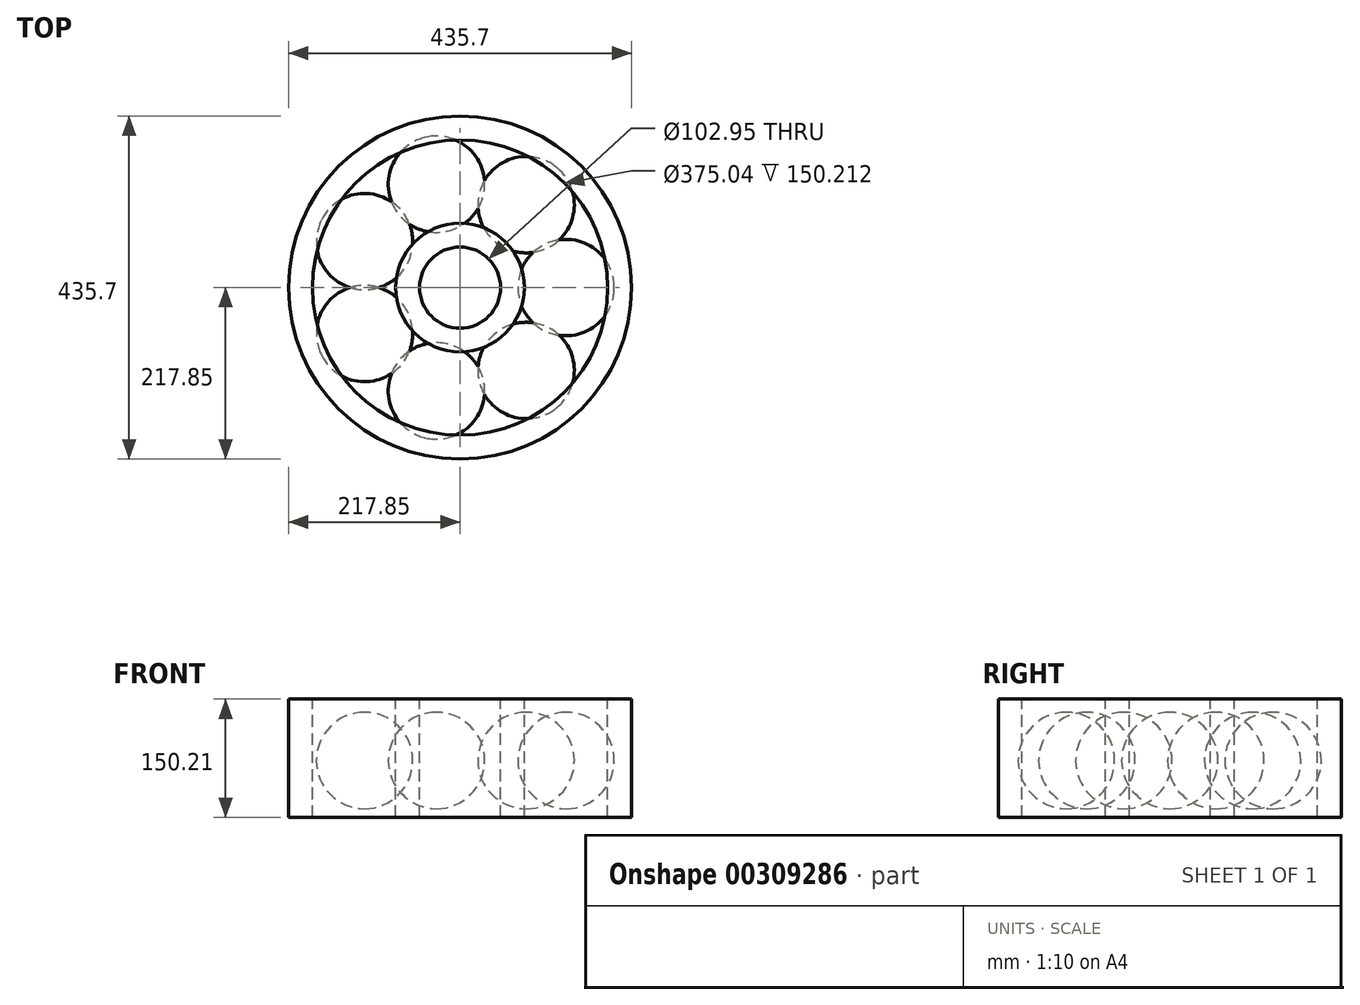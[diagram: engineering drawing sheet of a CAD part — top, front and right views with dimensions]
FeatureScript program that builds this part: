
annotation { "Feature Type Name" : "Feature", "Feature Type Description" : "" }
export const myFeature = defineFeature(function(context is Context, id is Id, definition is map)
    precondition{}
    {
        {
            var Q0;
            Q0=qCreatedBy(makeId("Front.planeOp"),FACE);
            var sketch = newSketch(context, id + "F0", { "sketchPlane" : qUnion([Q0])});
            skLineSegment(sketch, "E0", {"start": v(0, 77.92) * mm, "end": v(0, -75.83) * mm, "construction": true});
            skLineSegment(sketch, "E1.bottom", {"start": v(51.47, 77.92) * mm, "end": v(81.8, 77.92) * mm});
            skLineSegment(sketch, "E1.top", {"start": v(51.47, -72.3) * mm, "end": v(81.8, -72.3) * mm});
            skLineSegment(sketch, "E1.left", {"start": v(51.47, 77.92) * mm, "end": v(51.47, -72.3) * mm});
            skLineSegment(sketch, "E1.right", {"start": v(81.8, 77.92) * mm, "end": v(81.8, -72.3) * mm});
            skCircle(sketch, "E2", {"center": v(134.66, 0) * mm, "radius": 61.22 * mm});
            skLineSegment(sketch, "E3", {"start": v(134.66, 78.92) * mm, "end": v(134.66, -76.56) * mm, "construction": true});
            skLineSegment(sketch, "E4.MirrorCS", {"start": v(187.52, 77.92) * mm, "end": v(187.52, -72.3) * mm});
            skLineSegment(sketch, "E5.MirrorCS", {"start": v(217.85, 77.92) * mm, "end": v(187.52, 77.92) * mm});
            skLineSegment(sketch, "E6.MirrorCS", {"start": v(217.85, 77.92) * mm, "end": v(217.85, -72.3) * mm});
            skLineSegment(sketch, "E7.MirrorCS", {"start": v(217.85, -72.3) * mm, "end": v(187.52, -72.3) * mm});
            skLineSegment(sketch, "E8", {"start": v(134.66, 61.22) * mm, "end": v(134.66, -61.22) * mm});
            skSolve(sketch);
        }
        {
            var Q0;
            {var subQ1=sQuery(id+"F0.wireOp",EDGE,"E1.bottom");Q0=makeQuery(id+"F0.imprint","IMPRINT",FACE,{"disambiguationData":[TD([[makeQuery(id+"F0.imprint","IMPRINT",EDGE,{"derivedFrom":subQ1}),-1.0]])]});}
            var Q1;
            {var subQ0=sQuery(id+"F0.wireOp",EDGE,"E2");var subQ1=sQuery(id+"F0.wireOp",EDGE,"E1.right");var subQ2=makeQuery(id+"F0.imprint","INTERSECT",VERTEX,{"disambiguationData":[OD(0.0)],"derivedFrom":[subQ1,subQ0]});Q1=makeQuery(id+"F0.imprint","IMPRINT",FACE,{"disambiguationData":[TD([[makeQuery(id+"F0.imprint","IMPRINT",EDGE,{"disambiguationData":[TD([[subQ2,-1.0]])],"derivedFrom":subQ1}),-1.0]])]});}
            var Q2;
            {var subQ0=sQuery(id+"F0.wireOp",EDGE,"E5.MirrorCS");Q2=makeQuery(id+"F0.imprint","IMPRINT",FACE,{"disambiguationData":[TD([[makeQuery(id+"F0.imprint","IMPRINT",EDGE,{"derivedFrom":subQ0}),1.0]])]});}
            var Q3;
            {var subQ0=sQuery(id+"F0.wireOp",EDGE,"E4.MirrorCS");var subQ1=sQuery(id+"F0.wireOp",EDGE,"E2");var subQ2=makeQuery(id+"F0.imprint","INTERSECT",VERTEX,{"disambiguationData":[OD(0.0)],"derivedFrom":[subQ1,subQ0]});Q3=makeQuery(id+"F0.imprint","IMPRINT",FACE,{"disambiguationData":[TD([[makeQuery(id+"F0.imprint","IMPRINT",EDGE,{"disambiguationData":[TD([[subQ2,1.0]])],"derivedFrom":subQ1}),1.0]])]});}
            var Q4;
            Q4=sQuery(id+"F0.wireOp",EDGE,"E0");
            revolve(context, id + "F1", {"entities" : qUnion([Q0, Q1, Q2, Q3]), "axis" : qUnion([Q4]), "revolveType" : RevolveType.FULL});
        }
        {
            var Q0;
            {var subQ4=sQuery(id+"F0.wireOp",EDGE,"E8");Q0=makeQuery(id+"F0.imprint","IMPRINT",FACE,{"disambiguationData":[TD([[makeQuery(id+"F0.imprint","IMPRINT",EDGE,{"derivedFrom":subQ4}),-1.0]])]});}
            var Q1;
            {var subQ0=sQuery(id+"F0.wireOp",EDGE,"E2");var subQ1=sQuery(id+"F0.wireOp",EDGE,"E1.right");var subQ2=makeQuery(id+"F0.imprint","INTERSECT",VERTEX,{"disambiguationData":[OD(0.0)],"derivedFrom":[subQ1,subQ0]});Q1=makeQuery(id+"F0.imprint","IMPRINT",FACE,{"disambiguationData":[TD([[makeQuery(id+"F0.imprint","IMPRINT",EDGE,{"disambiguationData":[TD([[subQ2,-1.0]])],"derivedFrom":subQ1}),-1.0]])]});}
            var Q2;
            Q2=sQuery(id+"F0.wireOp",EDGE,"E8");
            revolve(context, id + "F2", {"entities" : qUnion([Q0, Q1]), "axis" : qUnion([Q2]), "revolveType" : RevolveType.FULL});
        }
        {
            var Q0;
            Q0=makeQuery(id+"F2.opRevolve","SWEPT_BODY",BODY,{"disambiguationData":[OSD([sQuery(id+"F0.wireOp",EDGE,"E1.right"),sQuery(id+"F0.wireOp",EDGE,"E2"),sQuery(id+"F0.wireOp",EDGE,"E8")])]});
            var Q1;
            Q1=sQuery(id+"F0.wireOp",EDGE,"E0");
            circularPattern(context, id + "F3", {"entities" : qUnion([Q0]), "axis" : qUnion([Q1]), "angle" : 360 * degree, "instanceCount" : 7, "equalSpace" : true});
        }
    });
